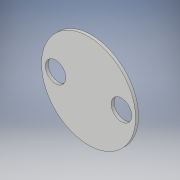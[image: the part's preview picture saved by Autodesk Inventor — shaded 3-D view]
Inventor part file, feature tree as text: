
AUTODESK INVENTOR PART (.ipt)
format: ipt  version: 2019.3 (Build 233278000, 278)  size: 101,376 bytes
history: native  units: in
note: dims shown in document units (in); Inventor stores cm internally (conversion verified against a paired STEP export)
features: extrude x1, sketch x1
ambient origin geometry x8: Origin, YZ Plane, XZ Plane, XY Plane, X Axis, Y Axis, Z Axis, Center Point
bodies: Solid1 (feature_tree)
feature tree (2):
  extrude  "Extrusion1"  Depth=0.125in
  sketch  "Sketch1"  dims[d0=0.875in d1=0.875in d2=2.8in d3=4.0in d4=0.125in d5=0.0in]
